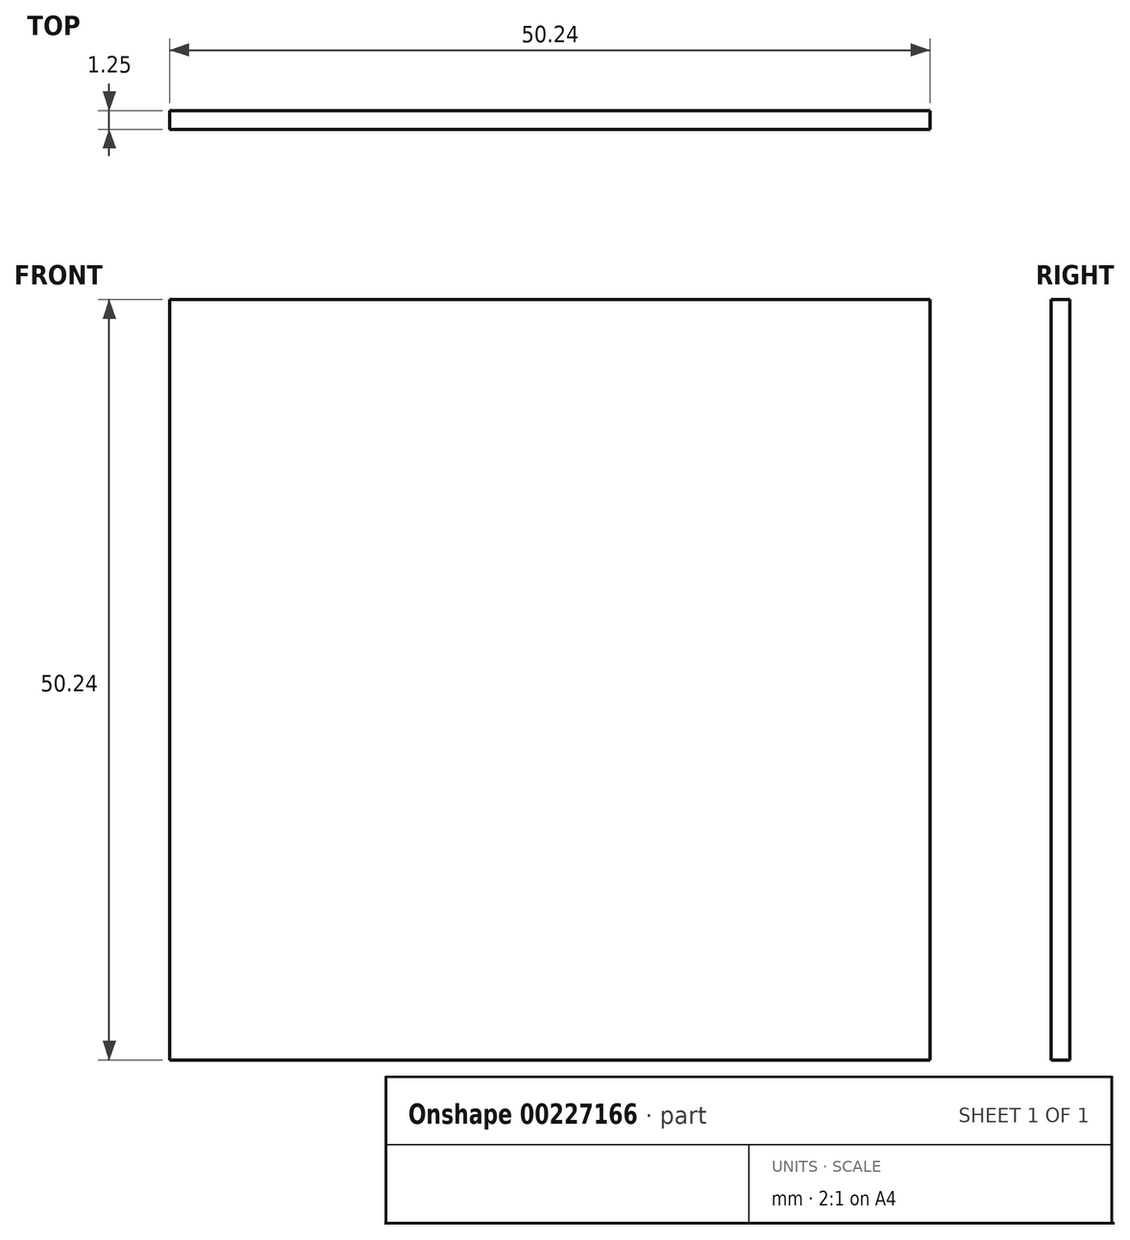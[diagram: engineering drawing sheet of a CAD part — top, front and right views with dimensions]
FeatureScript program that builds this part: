
annotation { "Feature Type Name" : "Feature", "Feature Type Description" : "" }
export const myFeature = defineFeature(function(context is Context, id is Id, definition is map)
    precondition{}
    {
        {
            var Q0;
            Q0=qCreatedBy(makeId("Front.planeOp"),FACE);
            var sketch = newSketch(context, id + "F0", { "sketchPlane" : qUnion([Q0])});
            skLineSegment(sketch, "E0.bottom", {"start": v(25.12, -25.12) * mm, "end": v(-25.12, -25.13) * mm});
            skLineSegment(sketch, "E0.top", {"start": v(25.12, 25.13) * mm, "end": v(-25.12, 25.12) * mm});
            skLineSegment(sketch, "E0.left", {"start": v(25.12, -25.12) * mm, "end": v(25.12, 25.13) * mm});
            skLineSegment(sketch, "E0.right", {"start": v(-25.12, -25.13) * mm, "end": v(-25.12, 25.12) * mm});
            skPoint(sketch, "E0.middle", {"position": v(0, 0) * mm});
            skSolve(sketch);
        }
        {
            var Q0;
            Q0 = qSketchRegion(id + "F0", true);
            extrude(context, id + "F1", {"entities" : qUnion([Q0]), "depth" : 1.25 * mm});
        }
    });
